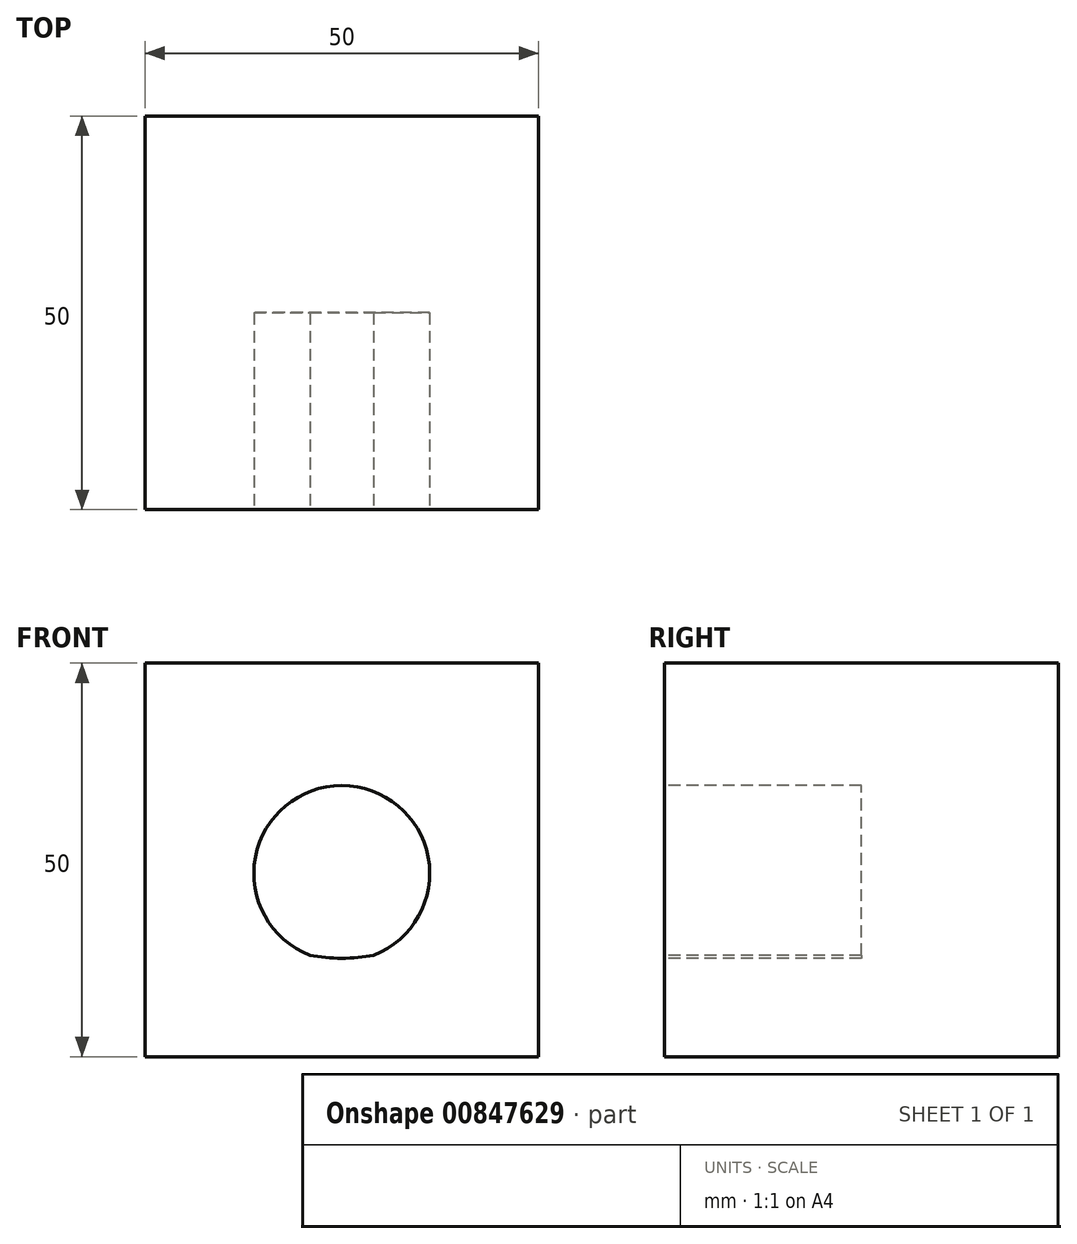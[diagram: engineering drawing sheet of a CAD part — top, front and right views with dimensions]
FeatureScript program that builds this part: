
annotation { "Feature Type Name" : "Feature", "Feature Type Description" : "" }
export const myFeature = defineFeature(function(context is Context, id is Id, definition is map)
    precondition{}
    {
        {
            var Q0;
            Q0=qCreatedBy(makeId("Top.planeOp"),FACE);
            var sketch = newSketch(context, id + "F0", { "sketchPlane" : qUnion([Q0])});
            skLineSegment(sketch, "E0.bottom", {"start": v(-25, -25) * mm, "end": v(25, -25) * mm});
            skLineSegment(sketch, "E0.top", {"start": v(-25, 25) * mm, "end": v(25, 25) * mm});
            skLineSegment(sketch, "E0.left", {"start": v(-25, -25) * mm, "end": v(-25, 25) * mm});
            skLineSegment(sketch, "E0.right", {"start": v(25, -25) * mm, "end": v(25, 25) * mm});
            skPoint(sketch, "E0.middle", {"position": v(0, 0) * mm});
            skSolve(sketch);
        }
        {
            var Q0;
            Q0 = qSketchRegion(id + "F0", true);
            var Q1;
            Q1=makeQuery(id+"F0.imprint","IMPRINT",FACE,{"disambiguationData":[TD([[makeQuery(id+"F0.imprint","IMPRINT",EDGE,{"derivedFrom":sQuery(id+"F0.wireOp",EDGE,"E0.bottom")}),1.0]])]});
            extrude(context, id + "F1", {"entities" : qUnion([Q0, Q1]), "depth" : 50 * mm, "offsetDistance" : 25 * mm});
        }
        {
            var Q0;
            Q0=makeQuery(id+"F1.opExtrude","SWEPT_FACE",FACE,{"disambiguationData":[OSD([sQuery(id+"F0.wireOp",EDGE,"E0.bottom")])]});
            var sketch = newSketch(context, id + "F2", { "sketchPlane" : qUnion([Q0])});
            skCircle(sketch, "E1", {"center": v(0, 23.28) * mm, "radius": 11.17 * mm});
            skArc(sketch, "E2", {"start": v(-4.06, 12.88) * mm, "mid": v(0, 12.5) * mm, "end": v(4.06, 12.88) * mm});
            skCircle(sketch, "E3", {"center": v(5.4, 49.27) * mm, "radius": 0.73 * mm});
            skSolve(sketch);
        }
        {
            var Q0;
            {var subQ0=sQuery(id+"F2.wireOp",EDGE,"E2");Q0=makeQuery(id+"F2.imprint","IMPRINT",FACE,{"disambiguationData":[TD([[makeQuery(id+"F2.imprint","IMPRINT",EDGE,{"derivedFrom":subQ0}),1.0]])]});}
            extrude(context, id + "F3", {"entities" : qUnion([Q0]), "operationType" : NewBodyOperationType.REMOVE, "oppositeDirection" : true, "depth" : 25 * mm, "offsetDistance" : 25 * mm});
        }
    });
